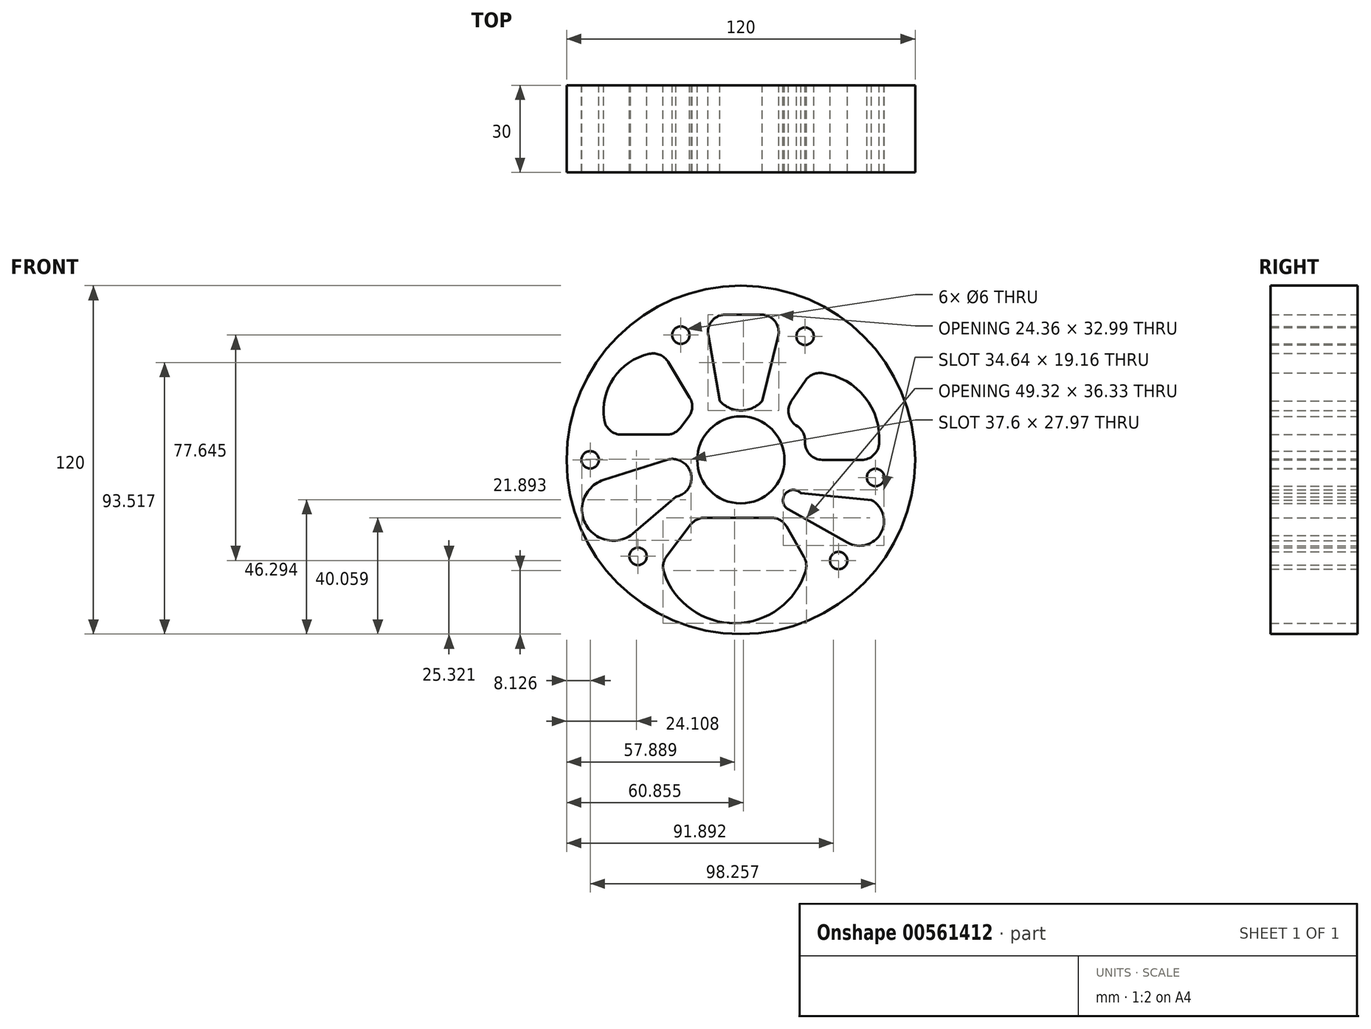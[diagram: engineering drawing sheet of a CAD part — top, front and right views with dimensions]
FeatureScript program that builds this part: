
annotation { "Feature Type Name" : "Feature", "Feature Type Description" : "" }
export const myFeature = defineFeature(function(context is Context, id is Id, definition is map)
    precondition{}
    {
        {
            var Q0;
            Q0=qCreatedBy(makeId("Front.planeOp"),FACE);
            var sketch = newSketch(context, id + "F0", { "sketchPlane" : qUnion([Q0])});
            skCircle(sketch, "E0", {"center": v(0, 0) * mm, "radius": 60 * mm});
            skCircle(sketch, "E1", {"center": v(0, 0) * mm, "radius": 15 * mm});
            skCircle(sketch, "E2", {"center": v(0, 0) * mm, "radius": 5.01 * mm});
            skLineSegment(sketch, "E3", {"start": v(4.84, 1.31) * mm, "end": v(7.14, 1.31) * mm});
            skLineSegment(sketch, "E4", {"start": v(7.14, -1.27) * mm, "end": v(4.85, -1.27) * mm});
            skLineSegment(sketch, "E5", {"start": v(1.48, -4.79) * mm, "end": v(1.48, -7.09) * mm});
            skLineSegment(sketch, "E6", {"start": v(-1.42, -7.09) * mm, "end": v(-1.42, -4.8) * mm});
            skLineSegment(sketch, "E7", {"start": v(1.48, 4.79) * mm, "end": v(1.48, 7.09) * mm});
            skLineSegment(sketch, "E8", {"start": v(-1.42, 7.09) * mm, "end": v(-1.42, 4.8) * mm});
            skLineSegment(sketch, "E9", {"start": v(-4.84, 1.31) * mm, "end": v(-7.14, 1.31) * mm});
            skLineSegment(sketch, "E10", {"start": v(-7.14, -1.27) * mm, "end": v(-4.85, -1.27) * mm});
            skPoint(sketch, "E11.visualSharp", {"position": v(1.48, 11.8) * mm});
            skArc(sketch, "E11.filletArc", {"start": v(1.48, 7.09) * mm, "mid": v(1.07, 8.3) * mm, "end": v(0.02, 9.01) * mm});
            skPoint(sketch, "E12.visualSharp", {"position": v(-1.42, 11.8) * mm});
            skArc(sketch, "E12.filletArc", {"start": v(0.02, 9.01) * mm, "mid": v(-1.02, 8.3) * mm, "end": v(-1.42, 7.09) * mm});
            skPoint(sketch, "E13.visualSharp", {"position": v(13.38, 1.31) * mm});
            skArc(sketch, "E13.filletArc", {"start": v(9.01, 0.03) * mm, "mid": v(8.28, 0.96) * mm, "end": v(7.14, 1.31) * mm});
            skPoint(sketch, "E14.visualSharp", {"position": v(13.38, -1.27) * mm});
            skArc(sketch, "E14.filletArc", {"start": v(7.14, -1.27) * mm, "mid": v(8.28, -0.92) * mm, "end": v(9.01, 0.03) * mm});
            skPoint(sketch, "E15.visualSharp", {"position": v(1.48, -11.46) * mm});
            skArc(sketch, "E15.filletArc", {"start": v(0.02, -9.01) * mm, "mid": v(1.07, -8.3) * mm, "end": v(1.48, -7.09) * mm});
            skPoint(sketch, "E16.visualSharp", {"position": v(-1.42, -11.46) * mm});
            skArc(sketch, "E16.filletArc", {"start": v(-1.42, -7.09) * mm, "mid": v(-1.02, -8.3) * mm, "end": v(0.02, -9.01) * mm});
            skPoint(sketch, "E17.visualSharp", {"position": v(-9.14, -1.27) * mm});
            skArc(sketch, "E17.filletArc", {"start": v(-9.01, 0.02) * mm, "mid": v(-8.28, -0.92) * mm, "end": v(-7.14, -1.27) * mm});
            skPoint(sketch, "E18.visualSharp", {"position": v(-9.14, 1.31) * mm});
            skArc(sketch, "E18.filletArc", {"start": v(-7.14, 1.31) * mm, "mid": v(-8.28, 0.96) * mm, "end": v(-9.01, 0.02) * mm});
            skCircle(sketch, "E19", {"center": v(7.31, 7.36) * mm, "radius": 2 * mm});
            skCircle(sketch, "E20", {"center": v(6.97, -6.13) * mm, "radius": 2 * mm});
            skCircle(sketch, "E21", {"center": v(0, -11.45) * mm, "radius": 2 * mm});
            skCircle(sketch, "E22", {"center": v(-7.2, -6.13) * mm, "radius": 2 * mm});
            skCircle(sketch, "E23", {"center": v(-7.2, 7.19) * mm, "radius": 2 * mm});
            skCircle(sketch, "E24", {"center": v(0, 12.17) * mm, "radius": 2 * mm});
            skLineSegment(sketch, "E25", {"start": v(7.31, 20.23) * mm, "end": v(12.86, 42.57) * mm});
            skLineSegment(sketch, "E26", {"start": v(7.04, 50.01) * mm, "end": v(-5.33, 50.01) * mm});
            skLineSegment(sketch, "E27", {"start": v(-11.24, 42.97) * mm, "end": v(-7.2, 20.23) * mm});
            skPoint(sketch, "E28.visualSharp", {"position": v(-12.5, 50.01) * mm});
            skArc(sketch, "E28.filletArc", {"start": v(-5.33, 50.01) * mm, "mid": v(-9.93, 47.87) * mm, "end": v(-11.24, 42.97) * mm});
            skPoint(sketch, "E29.visualSharp", {"position": v(14.71, 50.01) * mm});
            skArc(sketch, "E29.filletArc", {"start": v(12.86, 42.57) * mm, "mid": v(11.76, 47.7) * mm, "end": v(7.04, 50.01) * mm});
            skArc(sketch, "E30", {"start": v(-7.2, 20.23) * mm, "mid": v(0.05, 17.02) * mm, "end": v(7.31, 20.23) * mm});
            skCircle(sketch, "E31", {"center": v(22.1, 42.57) * mm, "radius": 3 * mm});
            skCircle(sketch, "E32", {"center": v(-20.66, 42.97) * mm, "radius": 3 * mm});
            skLineSegment(sketch, "E33", {"start": v(17.41, 20.26) * mm, "end": v(22.26, 27.33) * mm});
            skArc(sketch, "E34", {"start": v(47.56, 5.47) * mm, "mid": v(42.68, 21.61) * mm, "end": v(27.99, 29.88) * mm});
            skPoint(sketch, "E35.visualSharp", {"position": v(24.13, 30.06) * mm});
            skArc(sketch, "E35.filletArc", {"start": v(27.99, 29.88) * mm, "mid": v(24.76, 29.41) * mm, "end": v(22.26, 27.33) * mm});
            skLineSegment(sketch, "E36", {"start": v(18.96, 11.92) * mm, "end": v(19.5, 11.56) * mm});
            skLineSegment(sketch, "E37", {"start": v(22.1, 6.6) * mm, "end": v(22.1, 6) * mm});
            skLineSegment(sketch, "E38", {"start": v(28.1, 0) * mm, "end": v(41.59, 0) * mm});
            skPoint(sketch, "E39.visualSharp", {"position": v(14.02, 15.32) * mm});
            skArc(sketch, "E39.filletArc", {"start": v(17.41, 20.26) * mm, "mid": v(16.46, 15.77) * mm, "end": v(18.96, 11.92) * mm});
            skPoint(sketch, "E40.visualSharp", {"position": v(22.1, 0) * mm});
            skArc(sketch, "E40.filletArc", {"start": v(22.1, 6) * mm, "mid": v(23.86, 1.76) * mm, "end": v(28.1, 0) * mm});
            skPoint(sketch, "E41.visualSharp", {"position": v(22.1, 9.77) * mm});
            skArc(sketch, "E41.filletArc", {"start": v(22.1, 6.6) * mm, "mid": v(21.41, 9.4) * mm, "end": v(19.5, 11.56) * mm});
            skPoint(sketch, "E42.visualSharp", {"position": v(46.38, 0) * mm});
            skArc(sketch, "E42.filletArc", {"start": v(41.59, 0) * mm, "mid": v(45.64, 1.57) * mm, "end": v(47.56, 5.47) * mm});
            skCircle(sketch, "E43", {"center": v(46.38, -6.07) * mm, "radius": 3 * mm});
            skLineSegment(sketch, "E44", {"start": v(20.66, -11.46) * mm, "end": v(45, -13.83) * mm});
            skLineSegment(sketch, "E45", {"start": v(16.33, -17.05) * mm, "end": v(36.72, -28.5) * mm});
            skArc(sketch, "E46", {"start": v(20.66, -11.46) * mm, "mid": v(15.25, -11.74) * mm, "end": v(16.33, -17.05) * mm});
            skArc(sketch, "E47", {"start": v(36.72, -28.5) * mm, "mid": v(48.19, -25.3) * mm, "end": v(45, -13.83) * mm});
            skCircle(sketch, "E48", {"center": v(33.67, -34.68) * mm, "radius": 3 * mm});
            skLineSegment(sketch, "E49", {"start": v(10.52, -19.94) * mm, "end": v(-12.48, -19.94) * mm});
            skLineSegment(sketch, "E50", {"start": v(-17.26, -22.31) * mm, "end": v(-25.55, -33.23) * mm});
            skLineSegment(sketch, "E51", {"start": v(15.72, -22.95) * mm, "end": v(21.75, -33.46) * mm});
            skArc(sketch, "E52", {"start": v(-26.47, -38.76) * mm, "mid": v(-1.9, -56.27) * mm, "end": v(22.28, -38.21) * mm});
            skPoint(sketch, "E53.visualSharp", {"position": v(-15.46, -19.94) * mm});
            skArc(sketch, "E53.filletArc", {"start": v(-12.48, -19.94) * mm, "mid": v(-15.15, -20.57) * mm, "end": v(-17.26, -22.31) * mm});
            skPoint(sketch, "E54.visualSharp", {"position": v(14, -19.94) * mm});
            skArc(sketch, "E54.filletArc", {"start": v(15.72, -22.95) * mm, "mid": v(13.52, -20.75) * mm, "end": v(10.52, -19.94) * mm});
            skPoint(sketch, "E55.visualSharp", {"position": v(-27.3, -35.55) * mm});
            skArc(sketch, "E55.filletArc", {"start": v(-25.55, -33.23) * mm, "mid": v(-26.7, -35.88) * mm, "end": v(-26.47, -38.76) * mm});
            skPoint(sketch, "E56.visualSharp", {"position": v(22.95, -35.55) * mm});
            skArc(sketch, "E56.filletArc", {"start": v(22.28, -38.21) * mm, "mid": v(22.51, -35.78) * mm, "end": v(21.75, -33.46) * mm});
            skCircle(sketch, "E57", {"center": v(-35.4, -33.23) * mm, "radius": 3 * mm});
            skLineSegment(sketch, "E58", {"start": v(-22.4, -12.72) * mm, "end": v(-38, -26) * mm});
            skLineSegment(sketch, "E59", {"start": v(-25.58, 0) * mm, "end": v(-47.25, -6.94) * mm});
            skArc(sketch, "E60", {"start": v(-22.4, -12.72) * mm, "mid": v(-17.2, -4.66) * mm, "end": v(-25.58, 0) * mm});
            skArc(sketch, "E61", {"start": v(-47.25, -6.94) * mm, "mid": v(-53.62, -21.8) * mm, "end": v(-38, -26) * mm});
            skCircle(sketch, "E62", {"center": v(-51.87, 0) * mm, "radius": 3 * mm});
            skLineSegment(sketch, "E63", {"start": v(-20.88, 10.98) * mm, "end": v(-18.01, 14.65) * mm});
            skLineSegment(sketch, "E64", {"start": v(-17.6, 21.46) * mm, "end": v(-25.07, 33.77) * mm});
            skLineSegment(sketch, "E65", {"start": v(-25.61, 8.67) * mm, "end": v(-41.1, 8.67) * mm});
            skArc(sketch, "E66", {"start": v(-31.5, 36.52) * mm, "mid": v(-43.77, 28.2) * mm, "end": v(-47.02, 13.73) * mm});
            skPoint(sketch, "E67.visualSharp", {"position": v(-15.46, 17.92) * mm});
            skArc(sketch, "E67.filletArc", {"start": v(-18.01, 14.65) * mm, "mid": v(-16.75, 18) * mm, "end": v(-17.6, 21.46) * mm});
            skPoint(sketch, "E68.visualSharp", {"position": v(-22.69, 8.67) * mm});
            skArc(sketch, "E68.filletArc", {"start": v(-25.61, 8.67) * mm, "mid": v(-22.98, 9.28) * mm, "end": v(-20.88, 10.98) * mm});
            skPoint(sketch, "E69.visualSharp", {"position": v(-45.52, 8.67) * mm});
            skArc(sketch, "E69.filletArc", {"start": v(-47.02, 13.73) * mm, "mid": v(-44.99, 10.1) * mm, "end": v(-41.1, 8.67) * mm});
            skPoint(sketch, "E70.visualSharp", {"position": v(-27.02, 37) * mm});
            skArc(sketch, "E70.filletArc", {"start": v(-25.07, 33.77) * mm, "mid": v(-27.84, 36.17) * mm, "end": v(-31.5, 36.52) * mm});
            skSolve(sketch);
        }
        {
            var Q0;
            Q0 = qSketchRegion(id + "F0", true);
            extrude(context, id + "F1", {"entities" : qUnion([Q0]), "depth" : 30 * mm, "offsetDistance" : 25 * mm});
        }
    });
